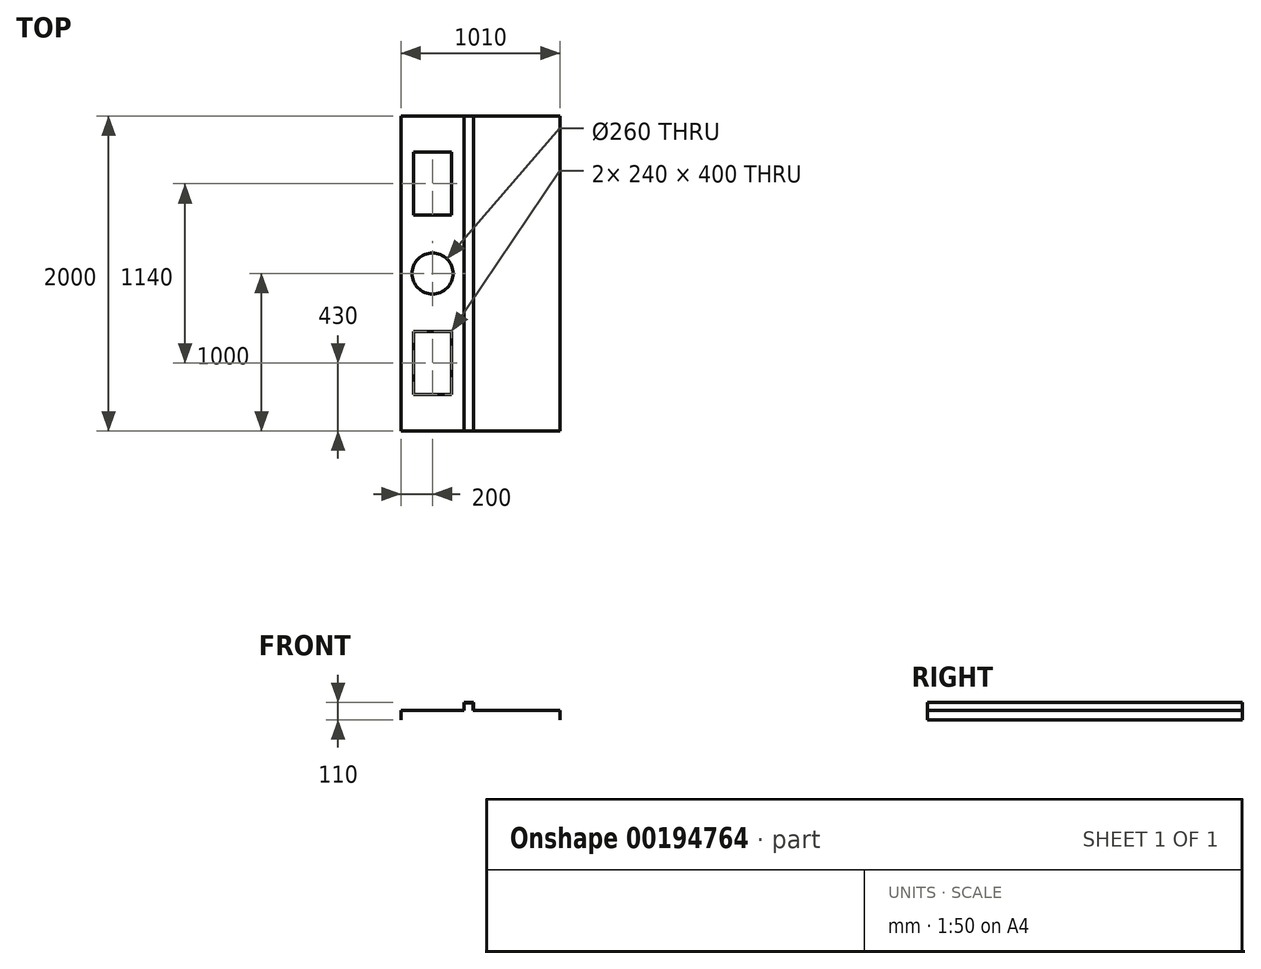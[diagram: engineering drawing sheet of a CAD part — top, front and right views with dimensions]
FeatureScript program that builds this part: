
annotation { "Feature Type Name" : "Feature", "Feature Type Description" : "" }
export const myFeature = defineFeature(function(context is Context, id is Id, definition is map)
    precondition{}
    {
        {
            var Q0;
            Q0=qCreatedBy(makeId("Front.planeOp"),FACE);
            var sketch = newSketch(context, id + "F0", { "sketchPlane" : qUnion([Q0])});
            skLineSegment(sketch, "E0", {"start": v(0, 0) * mm, "end": v(0, 60) * mm});
            skLineSegment(sketch, "E1", {"start": v(0, 60) * mm, "end": v(400, 60) * mm});
            skLineSegment(sketch, "E2", {"start": v(400, 60) * mm, "end": v(400, 110) * mm});
            skLineSegment(sketch, "E3", {"start": v(400, 110) * mm, "end": v(460, 110) * mm});
            skLineSegment(sketch, "E4", {"start": v(460, 110) * mm, "end": v(460, 60) * mm});
            skLineSegment(sketch, "E5", {"start": v(460, 60) * mm, "end": v(1010, 60) * mm});
            skLineSegment(sketch, "E6", {"start": v(1010, 60) * mm, "end": v(1010, 0) * mm});
            skLineSegment(sketch, "E7", {"start": v(1010, 0) * mm, "end": v(0, 0) * mm});
            skSolve(sketch);
        }
        {
            var Q0;
            Q0 = qSketchRegion(id + "F0", true);
            extrude(context, id + "F1", {"entities" : qUnion([Q0]), "depth" : 2000 * mm});
        }
        {
            var Q0;
            Q0=makeQuery(id+"F1.opExtrude","SWEPT_FACE",FACE,{"disambiguationData":[OSD([sQuery(id+"F0.wireOp",EDGE,"E7")])]});
            var Q1;
            Q1=makeQuery(id+"F1.opExtrude","CAP_FACE",FACE,{"disambiguationData":[OSD([sQuery(id+"F0.wireOp",EDGE,"E0"),sQuery(id+"F0.wireOp",EDGE,"E1"),sQuery(id+"F0.wireOp",EDGE,"E2"),sQuery(id+"F0.wireOp",EDGE,"E3"),sQuery(id+"F0.wireOp",EDGE,"E4"),sQuery(id+"F0.wireOp",EDGE,"E5"),sQuery(id+"F0.wireOp",EDGE,"E6"),sQuery(id+"F0.wireOp",EDGE,"E7")])],"isStart":false});
            var Q2;
            Q2=makeQuery(id+"F1.opExtrude","CAP_FACE",FACE,{"disambiguationData":[OSD([sQuery(id+"F0.wireOp",EDGE,"E0"),sQuery(id+"F0.wireOp",EDGE,"E1"),sQuery(id+"F0.wireOp",EDGE,"E2"),sQuery(id+"F0.wireOp",EDGE,"E3"),sQuery(id+"F0.wireOp",EDGE,"E4"),sQuery(id+"F0.wireOp",EDGE,"E5"),sQuery(id+"F0.wireOp",EDGE,"E6"),sQuery(id+"F0.wireOp",EDGE,"E7")])],"isStart":true});
            shell(context, id + "F2", {"entities" : qUnion([Q0, Q1, Q2]), "thickness" : 1.6 * mm});
        }
        {
            var Q0;
            Q0=makeQuery(id+"F1.opExtrude","SWEPT_FACE",FACE,{"disambiguationData":[OSD([sQuery(id+"F0.wireOp",EDGE,"E1")])]});
            var sketch = newSketch(context, id + "F3", { "sketchPlane" : qUnion([Q0])});
            skCircle(sketch, "E8", {"center": v(200, -1000) * mm, "radius": 130 * mm});
            skPoint(sketch, "E8.centerSnap0", {"position": v(200, 0) * mm});
            skPoint(sketch, "E8.centerSnap1", {"position": v(0, -1000) * mm});
            skLineSegment(sketch, "E9.bottom", {"start": v(320, -630) * mm, "end": v(80, -630) * mm});
            skLineSegment(sketch, "E9.top", {"start": v(320, -230) * mm, "end": v(80, -230) * mm});
            skLineSegment(sketch, "E9.left", {"start": v(320, -630) * mm, "end": v(320, -230) * mm});
            skLineSegment(sketch, "E9.right", {"start": v(80, -630) * mm, "end": v(80, -230) * mm});
            skPoint(sketch, "E9.middle", {"position": v(200, -430) * mm});
            skLineSegment(sketch, "E10.bottom", {"start": v(320, -1770) * mm, "end": v(80, -1770) * mm});
            skLineSegment(sketch, "E10.top", {"start": v(320, -1370) * mm, "end": v(80, -1370) * mm});
            skLineSegment(sketch, "E10.left", {"start": v(320, -1770) * mm, "end": v(320, -1370) * mm});
            skLineSegment(sketch, "E10.right", {"start": v(80, -1770) * mm, "end": v(80, -1370) * mm});
            skPoint(sketch, "E10.middle", {"position": v(200, -1570) * mm});
            skSolve(sketch);
        }
        {
            var Q0;
            Q0 = qSketchRegion(id + "F3", true);
            extrude(context, id + "F4", {"entities" : qUnion([Q0]), "operationType" : NewBodyOperationType.REMOVE, "endBound" : BoundingType.THROUGH_ALL, "oppositeDirection" : true, "depth" : 25 * mm});
        }
    });
